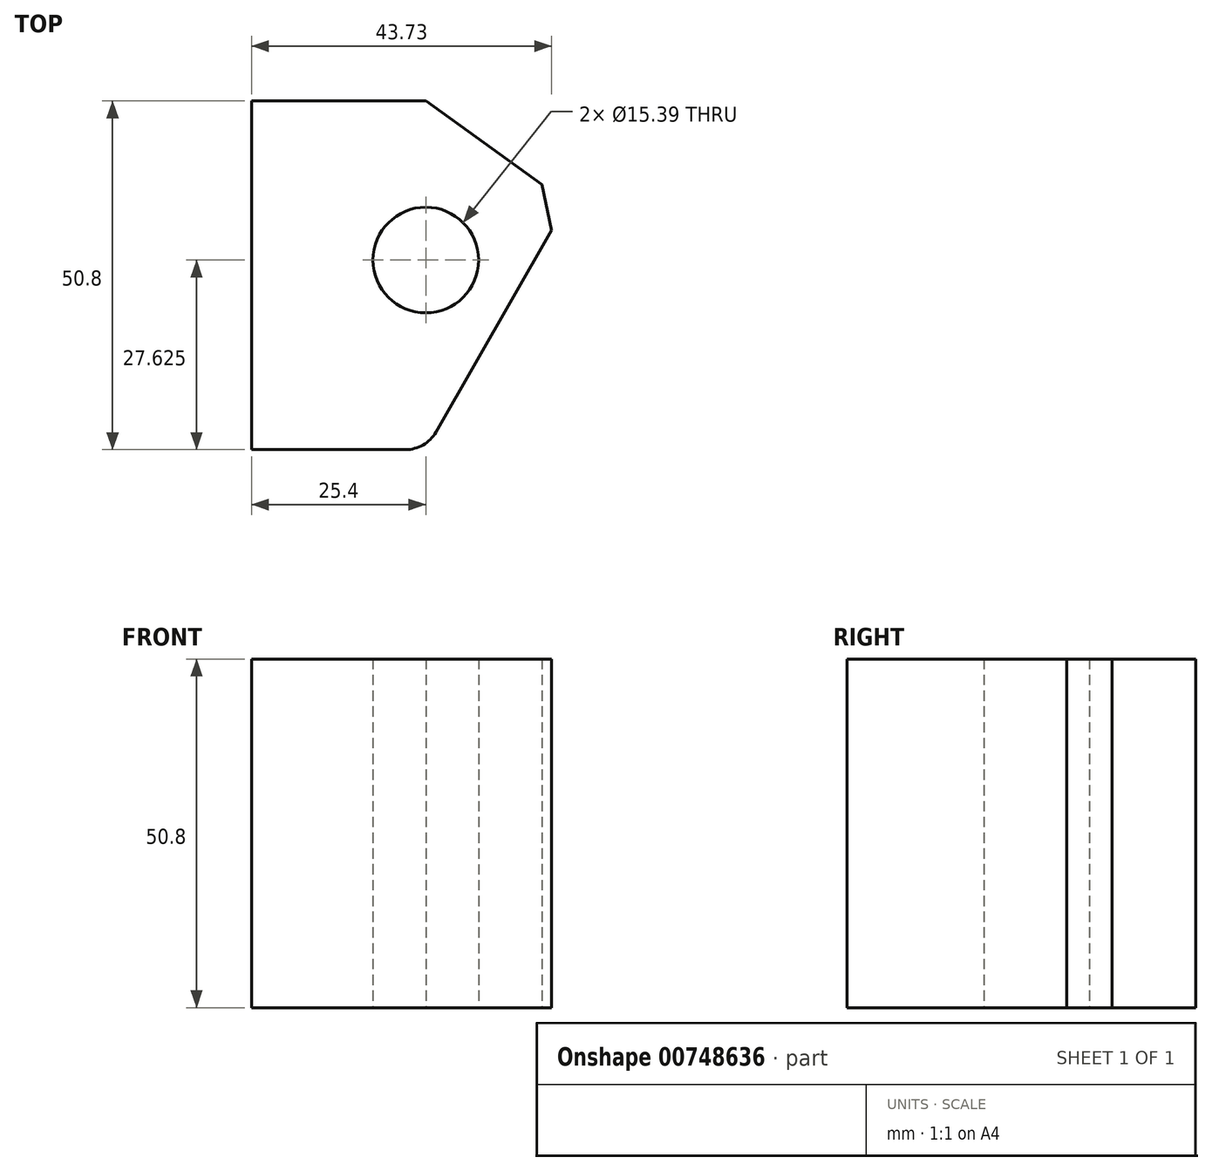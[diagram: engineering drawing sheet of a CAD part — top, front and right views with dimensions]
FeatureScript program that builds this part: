
annotation { "Feature Type Name" : "Feature", "Feature Type Description" : "" }
export const myFeature = defineFeature(function(context is Context, id is Id, definition is map)
    precondition{}
    {
        {
            var Q0;
            Q0=qCreatedBy(makeId("Top.planeOp"),FACE);
            var sketch = newSketch(context, id + "F0", { "sketchPlane" : qUnion([Q0])});
            skLineSegment(sketch, "E0.bottom", {"start": v(0, 0) * mm, "end": v(25.4, 0) * mm});
            skLineSegment(sketch, "E0.top", {"start": v(0, -50.8) * mm, "end": v(25.4, -50.8) * mm});
            skLineSegment(sketch, "E0.left", {"start": v(0, 0) * mm, "end": v(0, -50.8) * mm});
            skLineSegment(sketch, "E0.right", {"start": v(25.4, 0) * mm, "end": v(25.4, -50.8) * mm});
            skLineSegment(sketch, "E1", {"start": v(25.4, 0) * mm, "end": v(46, -14.85) * mm});
            skLineSegment(sketch, "E2", {"start": v(46, -14.85) * mm, "end": v(25.4, -50.8) * mm});
            skCircle(sketch, "E3", {"center": v(25.4, -23.17) * mm, "radius": 7.7 * mm});
            skSolve(sketch);
        }
        {
            var Q0;
            Q0 = qSketchRegion(id + "F0", true);
            extrude(context, id + "F1", {"entities" : qUnion([Q0]), "depth" : 50.8 * mm, "offsetDistance" : 25.4 * mm});
        }
        {
            var Q0;
            Q0=makeQuery(id+"F1.opExtrude","SWEPT_EDGE",EDGE,{"disambiguationData":[OSD([sQuery(id+"F0.wireOp",EDGE,"E0.top"),sQuery(id+"F0.wireOp",EDGE,"E0.right"),sQuery(id+"F0.wireOp",EDGE,"E2")])]});
            fillet(context, id + "F2", {"entities" : qUnion([Q0]), "radius" : 5.08 * mm, "tangentPropagation" : true, "allowEdgeOverflow" : false});
        }
        {
            var Q0;
            Q0=makeQuery(id+"F1.opExtrude","SWEPT_EDGE",EDGE,{"disambiguationData":[OSD([sQuery(id+"F0.wireOp",EDGE,"E1"),sQuery(id+"F0.wireOp",EDGE,"E2")])]});
            chamfer(context, id + "F3", {"entities" : qUnion([Q0]), "width" : 5.08 * mm, "tangentPropagation" : true});
        }
    });
